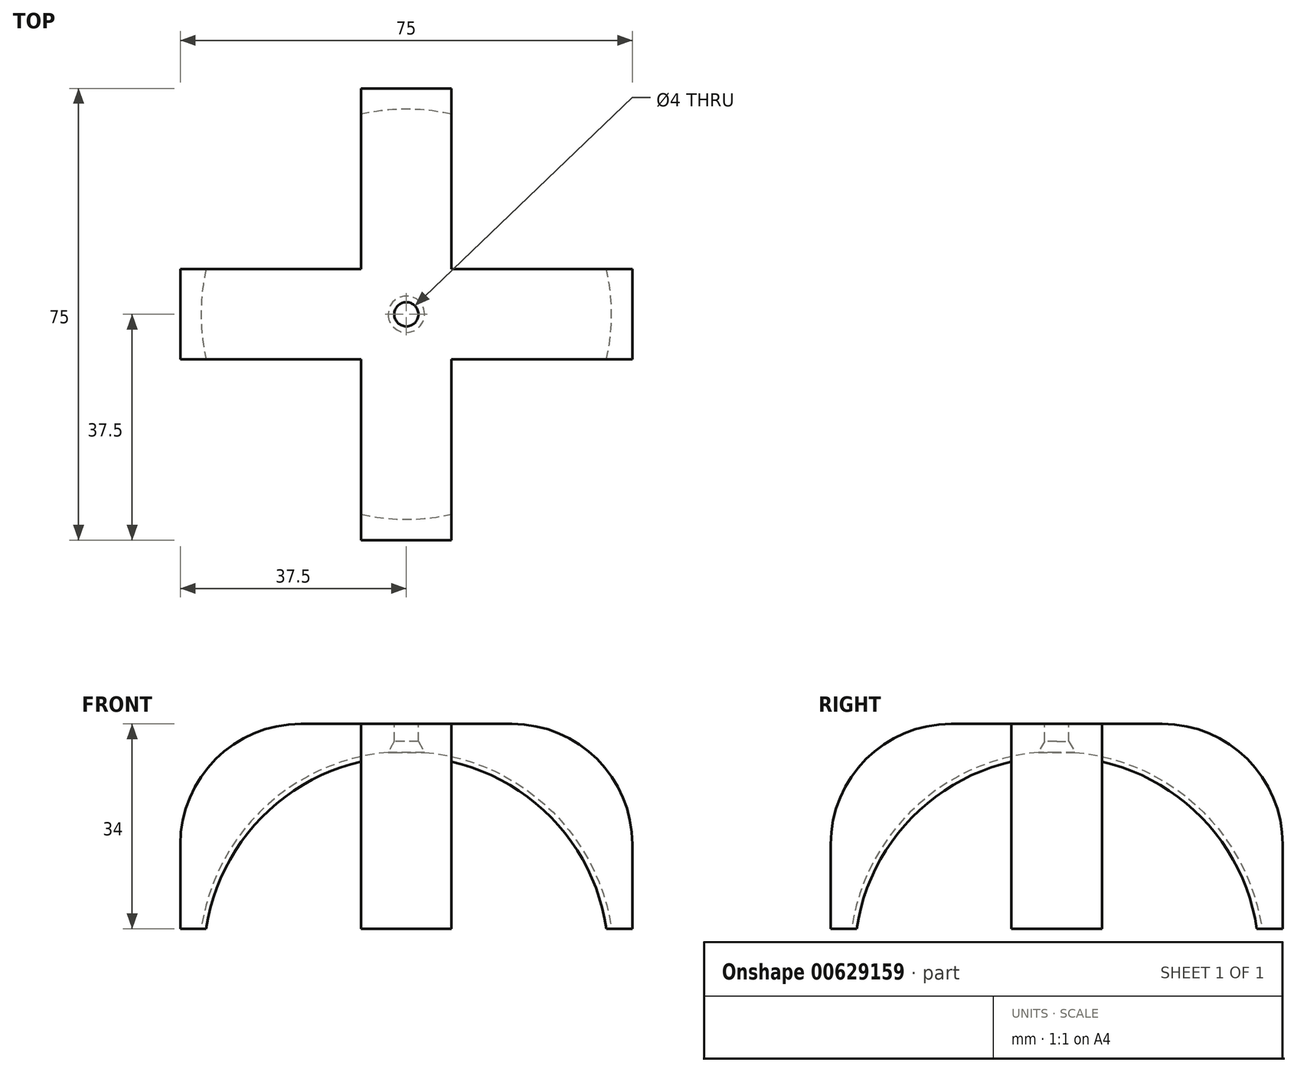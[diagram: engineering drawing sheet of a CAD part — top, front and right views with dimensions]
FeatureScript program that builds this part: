
annotation { "Feature Type Name" : "Feature", "Feature Type Description" : "" }
export const myFeature = defineFeature(function(context is Context, id is Id, definition is map)
    precondition{}
    {
        {
            var Q0;
            Q0=qCreatedBy(makeId("Top.planeOp"),FACE);
            var sketch = newSketch(context, id + "F0", { "sketchPlane" : qUnion([Q0])});
            skLineSegment(sketch, "E0.bottom", {"start": v(37.5, 7.5) * mm, "end": v(-37.5, 7.5) * mm});
            skLineSegment(sketch, "E0.top", {"start": v(37.5, -7.5) * mm, "end": v(-37.5, -7.5) * mm});
            skLineSegment(sketch, "E0.left", {"start": v(37.5, 7.5) * mm, "end": v(37.5, -7.5) * mm});
            skLineSegment(sketch, "E0.right", {"start": v(-37.5, 7.5) * mm, "end": v(-37.5, -7.5) * mm});
            skPoint(sketch, "E0.middle", {"position": v(0, 0) * mm});
            skLineSegment(sketch, "E1.bottom", {"start": v(-7.5, -37.5) * mm, "end": v(7.5, -37.5) * mm});
            skLineSegment(sketch, "E1.top", {"start": v(-7.5, 37.5) * mm, "end": v(7.5, 37.5) * mm});
            skLineSegment(sketch, "E1.left", {"start": v(-7.5, -37.5) * mm, "end": v(-7.5, 37.5) * mm});
            skLineSegment(sketch, "E1.right", {"start": v(7.5, -37.5) * mm, "end": v(7.5, 37.5) * mm});
            skCircle(sketch, "E2", {"center": v(0, 0) * mm, "radius": 34.3 * mm, "construction": true});
            skCircle(sketch, "E3", {"center": v(0, 0) * mm, "radius": 2 * mm});
            skSolve(sketch);
        }
        {
            var Q0;
            {var subQ5=sQuery(id+"F0.wireOp",EDGE,"E1.top");Q0=makeQuery(id+"F0.imprint","IMPRINT",FACE,{"disambiguationData":[TD([[makeQuery(id+"F0.imprint","IMPRINT",EDGE,{"derivedFrom":subQ5}),-1.0]])]});}
            var Q1;
            {var subQ0=sQuery(id+"F0.wireOp",EDGE,"E0.right");Q1=makeQuery(id+"F0.imprint","IMPRINT",FACE,{"disambiguationData":[TD([[makeQuery(id+"F0.imprint","IMPRINT",EDGE,{"derivedFrom":subQ0}),1.0]])]});}
            var Q2;
            Q2=makeQuery(id+"F0.imprint","IMPRINT",FACE,{"disambiguationData":[TD([[makeQuery(id+"F0.imprint","IMPRINT",EDGE,{"derivedFrom":sQuery(id+"F0.wireOp",EDGE,"E3")}),-1.0]])]});
            var Q3;
            {var subQ5=sQuery(id+"F0.wireOp",EDGE,"E1.bottom");Q3=makeQuery(id+"F0.imprint","IMPRINT",FACE,{"disambiguationData":[TD([[makeQuery(id+"F0.imprint","IMPRINT",EDGE,{"derivedFrom":subQ5}),1.0]])]});}
            var Q4;
            {var subQ0=sQuery(id+"F0.wireOp",EDGE,"E0.left");Q4=makeQuery(id+"F0.imprint","IMPRINT",FACE,{"disambiguationData":[TD([[makeQuery(id+"F0.imprint","IMPRINT",EDGE,{"derivedFrom":subQ0}),-1.0]])]});}
            extrude(context, id + "F1", {"entities" : qUnion([Q0, Q1, Q2, Q3, Q4]), "oppositeDirection" : true, "depth" : 30 * mm, "offsetDistance" : 25 * mm});
        }
        {
            var Q0;
            Q0=makeQuery(id+"F1.opExtrude","CAP_FACE",FACE,{"disambiguationData":[OSD([sQuery(id+"F0.wireOp",EDGE,"E0.bottom"),sQuery(id+"F0.wireOp",EDGE,"E0.top"),sQuery(id+"F0.wireOp",EDGE,"E0.left"),sQuery(id+"F0.wireOp",EDGE,"E0.right"),sQuery(id+"F0.wireOp",EDGE,"E1.bottom"),sQuery(id+"F0.wireOp",EDGE,"E1.top"),sQuery(id+"F0.wireOp",EDGE,"E1.left"),sQuery(id+"F0.wireOp",EDGE,"E1.right"),sQuery(id+"F0.wireOp",EDGE,"E3")])],"isStart":true});
            extrude(context, id + "F2", {"entities" : qUnion([Q0]), "operationType" : NewBodyOperationType.ADD, "depth" : 4 * mm, "offsetDistance" : 25 * mm});
        }
        {
            var Q0;
            Q0=qCreatedBy(makeId("Top.planeOp"),FACE);
            cPlane(context, id + "F3", {"entities" : qUnion([Q0]), "cplaneType" : CPlaneType.OFFSET, "offset" : 35 * mm, "oppositeDirection" : true, "width" : 150 * mm, "height" : 150 * mm});
        }
        {
            var Q0;
            Q0=qCreatedBy(id+"F3.planeOp",FACE);
            var sketch = newSketch(context, id + "F4", { "sketchPlane" : qUnion([Q0])});
            skCircle(sketch, "E4", {"center": v(0, 0) * mm, "radius": 34.4 * mm});
            skLineSegment(sketch, "E5", {"start": v(-24.04, -24.6) * mm, "end": v(24.03, 24.62) * mm});
            skSolve(sketch);
        }
        {
            var Q0;
            {var subQ0=sQuery(id+"F4.wireOp",EDGE,"E5");Q0=makeQuery(id+"F4.imprint","IMPRINT",FACE,{"disambiguationData":[TD([[makeQuery(id+"F4.imprint","IMPRINT",EDGE,{"derivedFrom":subQ0}),-1.0]])]});}
            var Q1;
            Q1=sQuery(id+"F4.wireOp",EDGE,"E5");
            revolve(context, id + "F5", {"surfaceOperationType" : NewSurfaceOperationType.NEW, "entities" : qUnion([Q0]), "axis" : qUnion([Q1]), "revolveType" : RevolveType.FULL});
        }
        {
            var Q0;
            Q0=makeQuery(id+"F5.opRevolve","SWEPT_BODY",BODY,{"disambiguationData":[OSD([sQuery(id+"F4.wireOp",EDGE,"E4"),sQuery(id+"F4.wireOp",EDGE,"E5")])]});
            var Q1;
            Q1=makeQuery(id+"F1.opExtrude","SWEPT_BODY",BODY,{"disambiguationData":[OSD([sQuery(id+"F0.wireOp",EDGE,"E0.bottom"),sQuery(id+"F0.wireOp",EDGE,"E0.top"),sQuery(id+"F0.wireOp",EDGE,"E0.left"),sQuery(id+"F0.wireOp",EDGE,"E0.right"),sQuery(id+"F0.wireOp",EDGE,"E1.bottom"),sQuery(id+"F0.wireOp",EDGE,"E1.top"),sQuery(id+"F0.wireOp",EDGE,"E1.left"),sQuery(id+"F0.wireOp",EDGE,"E1.right"),sQuery(id+"F0.wireOp",EDGE,"E3")])]});
            booleanBodies(context, id + "F6", {"operationType" : BooleanOperationType.SUBTRACTION, "tools" : qUnion([Q0]), "targets" : qUnion([Q1])});
        }
        {
            var Q0;
            Q0=makeQuery(id+"F2.opExtrude","CAP_FACE",FACE,{"disambiguationData":[OSD([sQuery(id+"F0.wireOp",EDGE,"E0.bottom"),sQuery(id+"F0.wireOp",EDGE,"E0.top"),sQuery(id+"F0.wireOp",EDGE,"E0.left"),sQuery(id+"F0.wireOp",EDGE,"E0.right"),sQuery(id+"F0.wireOp",EDGE,"E1.bottom"),sQuery(id+"F0.wireOp",EDGE,"E1.top"),sQuery(id+"F0.wireOp",EDGE,"E1.left"),sQuery(id+"F0.wireOp",EDGE,"E1.right"),sQuery(id+"F0.wireOp",EDGE,"E3")])],"isStart":false});
            cPlane(context, id + "F7", {"entities" : qUnion([Q0]), "cplaneType" : CPlaneType.OFFSET, "offset" : 6 * mm, "oppositeDirection" : true, "width" : 150 * mm, "height" : 150 * mm});
        }
        {
            var Q0;
            Q0=qCreatedBy(id+"F7.planeOp",FACE);
            var sketch = newSketch(context, id + "F8", { "sketchPlane" : qUnion([Q0])});
            skCircle(sketch, "E6", {"center": v(0, 0) * mm, "radius": 3.75 * mm});
            skSolve(sketch);
        }
        {
            var Q0;
            Q0=qCreatedBy(id+"F7.planeOp",FACE);
            cPlane(context, id + "F9", {"entities" : qUnion([Q0]), "cplaneType" : CPlaneType.OFFSET, "offset" : 4 * mm, "width" : 150 * mm, "height" : 150 * mm});
        }
        {
            var Q0;
            Q0=qCreatedBy(id+"F9.planeOp",FACE);
            var sketch = newSketch(context, id + "F10", { "sketchPlane" : qUnion([Q0])});
            skCircle(sketch, "E7", {"center": v(0, 0) * mm, "radius": 1.5 * mm});
            skSolve(sketch);
        }
        {
            var Q1;
            Q1=makeQuery(id+"F10.imprint","IMPRINT",FACE,{"disambiguationData":[TD([[makeQuery(id+"F10.imprint","IMPRINT",EDGE,{"derivedFrom":sQuery(id+"F10.wireOp",EDGE,"E7")}),1.0]])]});
            var Q2;
            Q2=makeQuery(id+"F8.imprint","IMPRINT",FACE,{"disambiguationData":[TD([[makeQuery(id+"F8.imprint","IMPRINT",EDGE,{"derivedFrom":sQuery(id+"F8.wireOp",EDGE,"E6")}),1.0]])]});
            loft(context, id + "F11", {"sheetProfilesArray" : [{ "sheetProfileEntities" : qUnion([Q1]) }, { "sheetProfileEntities" : qUnion([Q2]) }]});
        }
        {
            var Q0;
            Q0=makeQuery(id+"F11.opLoft","SWEPT_BODY",BODY,{"disambiguationData":[OSD([makeQuery(id+"F8.imprint","IMPRINT",FACE,{"disambiguationData":[TD([[makeQuery(id+"F8.imprint","IMPRINT",EDGE,{"derivedFrom":sQuery(id+"F8.wireOp",EDGE,"E6")}),1.0]])]}),makeQuery(id+"F10.imprint","IMPRINT",FACE,{"disambiguationData":[TD([[makeQuery(id+"F10.imprint","IMPRINT",EDGE,{"derivedFrom":sQuery(id+"F10.wireOp",EDGE,"E7")}),1.0]])]})])]});
            var Q1;
            Q1=makeQuery(id+"F1.opExtrude","SWEPT_BODY",BODY,{"disambiguationData":[OSD([sQuery(id+"F0.wireOp",EDGE,"E0.bottom"),sQuery(id+"F0.wireOp",EDGE,"E0.top"),sQuery(id+"F0.wireOp",EDGE,"E0.left"),sQuery(id+"F0.wireOp",EDGE,"E0.right"),sQuery(id+"F0.wireOp",EDGE,"E1.bottom"),sQuery(id+"F0.wireOp",EDGE,"E1.top"),sQuery(id+"F0.wireOp",EDGE,"E1.left"),sQuery(id+"F0.wireOp",EDGE,"E1.right"),sQuery(id+"F0.wireOp",EDGE,"E3")])]});
            booleanBodies(context, id + "F12", {"operationType" : BooleanOperationType.SUBTRACTION, "tools" : qUnion([Q0]), "targets" : qUnion([Q1])});
        }
        {
            var Q0;
            Q0=makeQuery(id+"F2.opExtrude","CAP_EDGE",EDGE,{"disambiguationData":[OSD([sQuery(id+"F0.wireOp",EDGE,"E0.right")])],"isStart":false});
            var Q1;
            Q1=makeQuery(id+"F2.opExtrude","CAP_EDGE",EDGE,{"disambiguationData":[OSD([sQuery(id+"F0.wireOp",EDGE,"E1.top")])],"isStart":false});
            var Q2;
            Q2=makeQuery(id+"F2.opExtrude","CAP_EDGE",EDGE,{"disambiguationData":[OSD([sQuery(id+"F0.wireOp",EDGE,"E0.left")])],"isStart":false});
            var Q3;
            Q3=makeQuery(id+"F2.opExtrude","CAP_EDGE",EDGE,{"disambiguationData":[OSD([sQuery(id+"F0.wireOp",EDGE,"E1.bottom")])],"isStart":false});
            fillet(context, id + "F13", {"entities" : qUnion([Q0, Q1, Q2, Q3]), "radius" : 20 * mm, "tangentPropagation" : true, "allowEdgeOverflow" : false});
        }
    });
